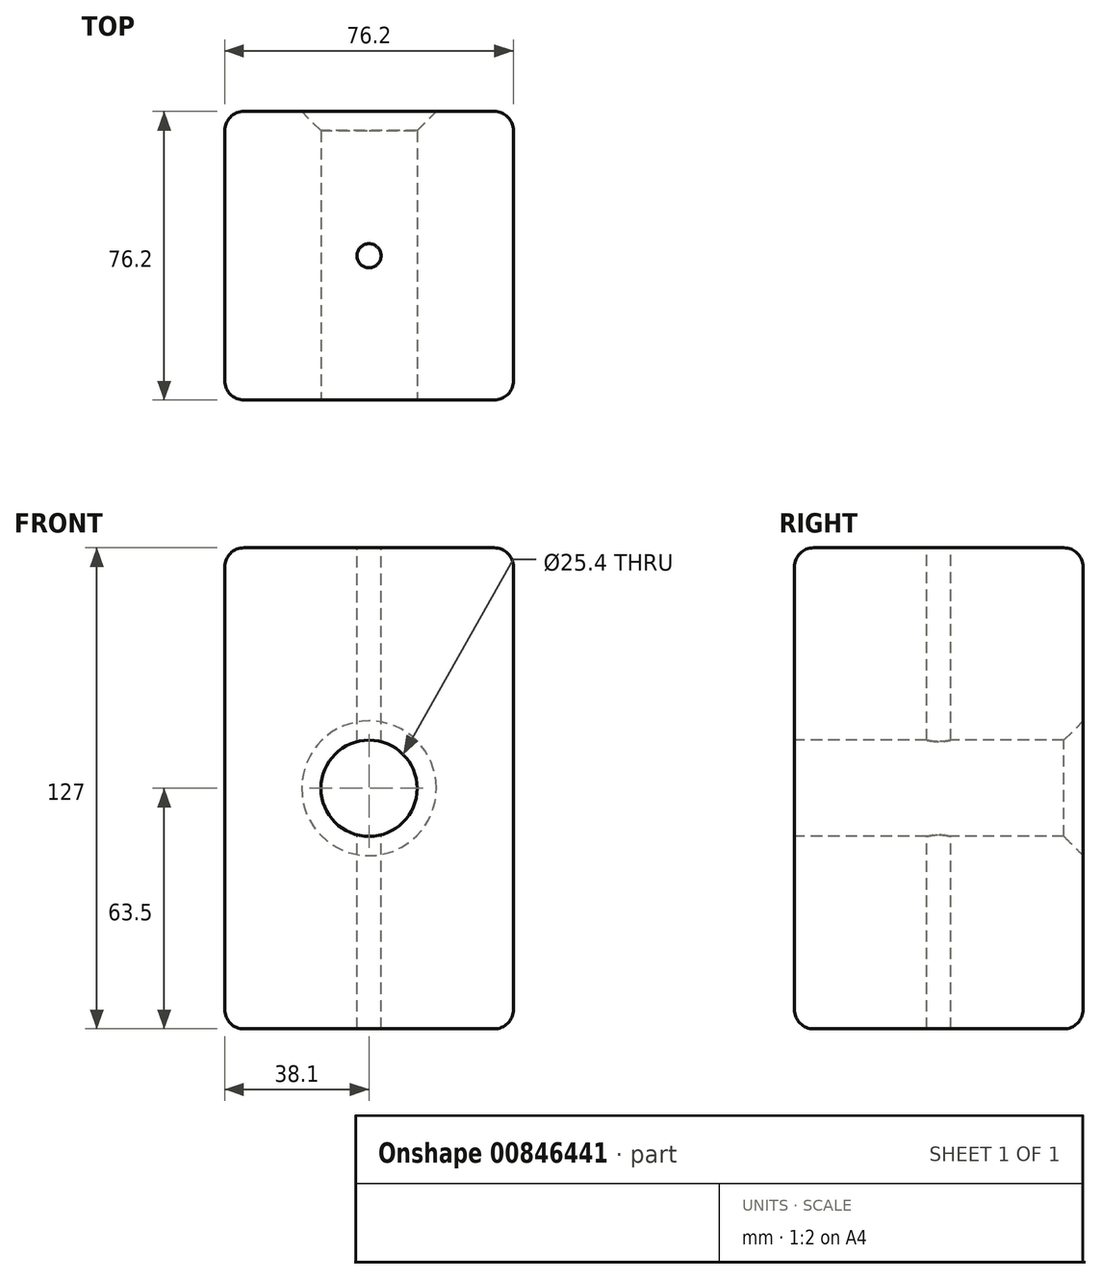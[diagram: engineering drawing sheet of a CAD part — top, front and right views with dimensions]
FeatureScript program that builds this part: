
annotation { "Feature Type Name" : "Feature", "Feature Type Description" : "" }
export const myFeature = defineFeature(function(context is Context, id is Id, definition is map)
    precondition{}
    {
        {
            var Q0;
            Q0=qCreatedBy(makeId("Top.planeOp"),FACE);
            var sketch = newSketch(context, id + "F0", { "sketchPlane" : qUnion([Q0])});
            skLineSegment(sketch, "E0.bottom", {"start": v(38.1, 38.1) * mm, "end": v(-38.1, 38.1) * mm});
            skLineSegment(sketch, "E0.top", {"start": v(38.1, -38.1) * mm, "end": v(-38.1, -38.1) * mm});
            skLineSegment(sketch, "E0.left", {"start": v(38.1, 38.1) * mm, "end": v(38.1, -38.1) * mm});
            skLineSegment(sketch, "E0.right", {"start": v(-38.1, 38.1) * mm, "end": v(-38.1, -38.1) * mm});
            skPoint(sketch, "E0.middle", {"position": v(0, 0) * mm});
            skSolve(sketch);
        }
        {
            var Q0;
            Q0=makeQuery(id+"F0.imprint","IMPRINT",FACE,{"disambiguationData":[TD([[makeQuery(id+"F0.imprint","IMPRINT",EDGE,{"derivedFrom":sQuery(id+"F0.wireOp",EDGE,"E0.bottom")}),1.0]])]});
            extrude(context, id + "F1", {"entities" : qUnion([Q0]), "depth" : 127 * mm, "offsetDistance" : 25.4 * mm});
        }
        {
            var Q0;
            Q0=makeQuery(id+"F1.opExtrude","SWEPT_FACE",FACE,{"disambiguationData":[OSD([sQuery(id+"F0.wireOp",EDGE,"E0.top")])]});
            var sketch = newSketch(context, id + "F2", { "sketchPlane" : qUnion([Q0])});
            skCircle(sketch, "E1", {"center": v(0, 63.5) * mm, "radius": 12.7 * mm});
            skPoint(sketch, "E1.centerSnap0", {"position": v(38.1, 63.5) * mm});
            skPoint(sketch, "E1.centerSnap1", {"position": v(0, 127) * mm});
            skSolve(sketch);
        }
        {
            var Q0;
            Q0 = qSketchRegion(id + "F2", true);
            extrude(context, id + "F3", {"entities" : qUnion([Q0]), "operationType" : NewBodyOperationType.REMOVE, "endBound" : BoundingType.THROUGH_ALL, "oppositeDirection" : true, "depth" : 25.4 * mm, "offsetDistance" : 25.4 * mm});
        }
        {
            var Q0;
            Q0=makeQuery(id+"F3.boolean.opBoolean","COPY",EDGE,{"derivedFrom":makeQuery(id+"F3.opExtrude","CAP_EDGE",EDGE,{"disambiguationData":[OSD([sQuery(id+"F2.wireOp",EDGE,"E1")])],"isStart":true})});
            var Q1;
            Q1=makeQuery(id+"F3.boolean.opBoolean","INTERSECT",EDGE,{"derivedFrom":[makeQuery(id+"F1.opExtrude","SWEPT_FACE",FACE,{"disambiguationData":[OSD([sQuery(id+"F0.wireOp",EDGE,"E0.bottom")])]}),makeQuery(id+"F3.opExtrude","SWEPT_FACE",FACE,{"disambiguationData":[OSD([sQuery(id+"F2.wireOp",EDGE,"E1")])]})]});
            chamfer(context, id + "F4", {"entities" : qUnion([Q0, Q1]), "width" : 5.08 * mm, "tangentPropagation" : true});
        }
        {
            var Q0;
            Q0=makeQuery(id+"F1.opExtrude","CAP_EDGE",EDGE,{"disambiguationData":[OSD([sQuery(id+"F0.wireOp",EDGE,"E0.top")])],"isStart":false});
            var Q1;
            Q1=makeQuery(id+"F1.opExtrude","CAP_EDGE",EDGE,{"disambiguationData":[OSD([sQuery(id+"F0.wireOp",EDGE,"E0.left")])],"isStart":false});
            var Q2;
            Q2=makeQuery(id+"F1.opExtrude","CAP_EDGE",EDGE,{"disambiguationData":[OSD([sQuery(id+"F0.wireOp",EDGE,"E0.bottom")])],"isStart":false});
            var Q3;
            Q3=makeQuery(id+"F1.opExtrude","CAP_EDGE",EDGE,{"disambiguationData":[OSD([sQuery(id+"F0.wireOp",EDGE,"E0.right")])],"isStart":false});
            var Q4;
            Q4=makeQuery(id+"F1.opExtrude","CAP_EDGE",EDGE,{"disambiguationData":[OSD([sQuery(id+"F0.wireOp",EDGE,"E0.right")])],"isStart":true});
            var Q5;
            Q5=makeQuery(id+"F1.opExtrude","CAP_EDGE",EDGE,{"disambiguationData":[OSD([sQuery(id+"F0.wireOp",EDGE,"E0.left")])],"isStart":true});
            var Q6;
            Q6=makeQuery(id+"F1.opExtrude","CAP_EDGE",EDGE,{"disambiguationData":[OSD([sQuery(id+"F0.wireOp",EDGE,"E0.bottom")])],"isStart":true});
            var Q7;
            Q7=makeQuery(id+"F1.opExtrude","CAP_EDGE",EDGE,{"disambiguationData":[OSD([sQuery(id+"F0.wireOp",EDGE,"E0.top")])],"isStart":true});
            var Q8;
            Q8=makeQuery(id+"F1.opExtrude","SWEPT_EDGE",EDGE,{"disambiguationData":[OSD([sQuery(id+"F0.wireOp",EDGE,"E0.top"),sQuery(id+"F0.wireOp",EDGE,"E0.left")])]});
            var Q9;
            Q9=makeQuery(id+"F1.opExtrude","SWEPT_EDGE",EDGE,{"disambiguationData":[OSD([sQuery(id+"F0.wireOp",EDGE,"E0.bottom"),sQuery(id+"F0.wireOp",EDGE,"E0.left")])]});
            var Q10;
            Q10=makeQuery(id+"F1.opExtrude","SWEPT_EDGE",EDGE,{"disambiguationData":[OSD([sQuery(id+"F0.wireOp",EDGE,"E0.bottom"),sQuery(id+"F0.wireOp",EDGE,"E0.right")])]});
            var Q11;
            Q11=makeQuery(id+"F1.opExtrude","SWEPT_EDGE",EDGE,{"disambiguationData":[OSD([sQuery(id+"F0.wireOp",EDGE,"E0.top"),sQuery(id+"F0.wireOp",EDGE,"E0.right")])]});
            fillet(context, id + "F5", {"entities" : qUnion([Q0, Q1, Q2, Q3, Q4, Q5, Q6, Q7, Q8, Q9, Q10, Q11]), "radius" : 5.08 * mm, "tangentPropagation" : true, "allowEdgeOverflow" : false});
        }
        {
            var Q0;
            Q0=makeQuery(id+"F1.opExtrude","CAP_FACE",FACE,{"disambiguationData":[OSD([sQuery(id+"F0.wireOp",EDGE,"E0.bottom"),sQuery(id+"F0.wireOp",EDGE,"E0.top"),sQuery(id+"F0.wireOp",EDGE,"E0.left"),sQuery(id+"F0.wireOp",EDGE,"E0.right")])],"isStart":false});
            var sketch = newSketch(context, id + "F6", { "sketchPlane" : qUnion([Q0])});
            skPoint(sketch, "E2", {"position": v(0, 0) * mm});
            skSolve(sketch);
        }
        {
            var Q0;
            Q0=sQuery(id+"F6.wireOp",VERTEX,"E2");
            var Q1;
            Q1=makeQuery(id+"F1.opExtrude","SWEPT_BODY",BODY,{"disambiguationData":[OSD([sQuery(id+"F0.wireOp",EDGE,"E0.bottom"),sQuery(id+"F0.wireOp",EDGE,"E0.top"),sQuery(id+"F0.wireOp",EDGE,"E0.left"),sQuery(id+"F0.wireOp",EDGE,"E0.right")])]});
            hole(context, id + "F7", {"style" : HoleStyle.SIMPLE, "endStyle" : HoleEndStyle.THROUGH, "holeDiameter" : 6.35 * mm, "majorDiameter" : 6.35 * mm, "isTappedThrough" : true, "tappedDepth" : 12.7 * mm, "tapClearance" : 3, "locations" : qUnion([Q0]), "scope" : qUnion([Q1])});
        }
    });
